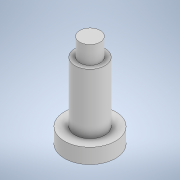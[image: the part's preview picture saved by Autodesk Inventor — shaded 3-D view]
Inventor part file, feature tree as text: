
AUTODESK INVENTOR PART (.ipt)
format: ipt  version: 2022 (Build 260153000, 153)  size: 111,616 bytes
history: native  units: mm
features: extrude x3, sketch x3
ambient origin geometry x8: Origin, YZ Plane, XZ Plane, XY Plane, X Axis, Y Axis, Z Axis, Center Point
bodies: Solid1 (feature_tree)
feature tree (6):
  extrude  "Extrusion1"  Depth=2.5mm TaperAngle=0.0deg
  extrude  "Extrusion2"  Depth=10.0mm TaperAngle=0.0deg
  extrude  "Extrusion3"  Depth=3.0mm TaperAngle=0.0deg
  sketch  "Sketch1"  dims[d0=8.5mm d1=2.5mm d2=0.0mm]
  sketch  "Sketch2"  dims[d3=5.0mm d4=10.0mm d5=0.0mm]
  sketch  "Sketch3"  dims[d6=3.4mm d7=3.0mm d8=0.0mm]
